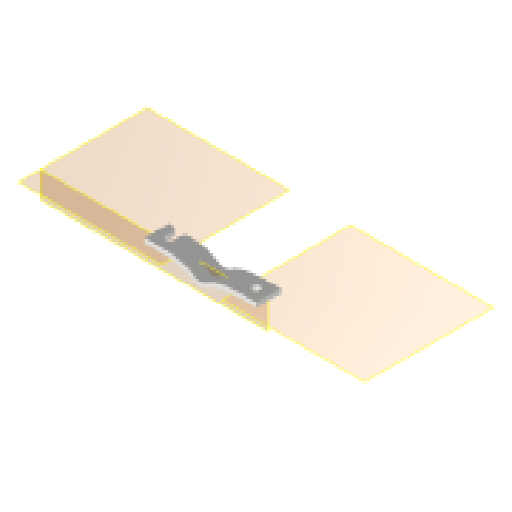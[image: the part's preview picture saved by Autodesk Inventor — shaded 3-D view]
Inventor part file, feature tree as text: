
AUTODESK INVENTOR PART (.ipt)
format: ipt  version: 2024.1 (Build 281209000, 209)  size: 182,784 bytes
history: native  units: mm
features: plane x3, extrude x3, sketch x3, other x2, mirror x1, fillet x1, reference x1
ambient origin geometry x8: Origin, YZ Plane, XZ Plane, XY Plane, X Axis, Y Axis, Z Axis, Center Point
bodies: Volumenkörper1 (feature_tree)
feature tree (14):
  plane  "Arbeitsebene1"
  extrude  "Extrusion1"  Depth=10.0mm
  plane  "Arbeitsebene2"
  extrude  "Extrusion2"  Depth=10.0mm TaperAngle=0.0deg
  mirror  "Spiegeln1"
  extrude  "Extrusion3"  [1 undecoded]
  fillet  "Rundung1"  [1 undecoded]
  sketch  "Skizze1"  dims[d0=10.0mm d1=0.0mm d2=3.2mm]
  sketch  "Skizze2"  dims[d3=10.0mm d4=0.0mm d5=10.0mm d6=0.0mm]
  reference  "Referenz2"
  plane  "Arbeitsebene3"
  sketch  "Skizze3"  dims[d7=2.0mm]
  other  "Assembly_Planktoscope_Uc2version_wormdrive_V3.iam"
  other  "60_Planktoscope_Sampleholder:1"
note: 2 required parameter values undecoded (feature->parameter linkage not recoverable at this tier; creation-order binding heuristic only, values carry confidence <= 0.55)
